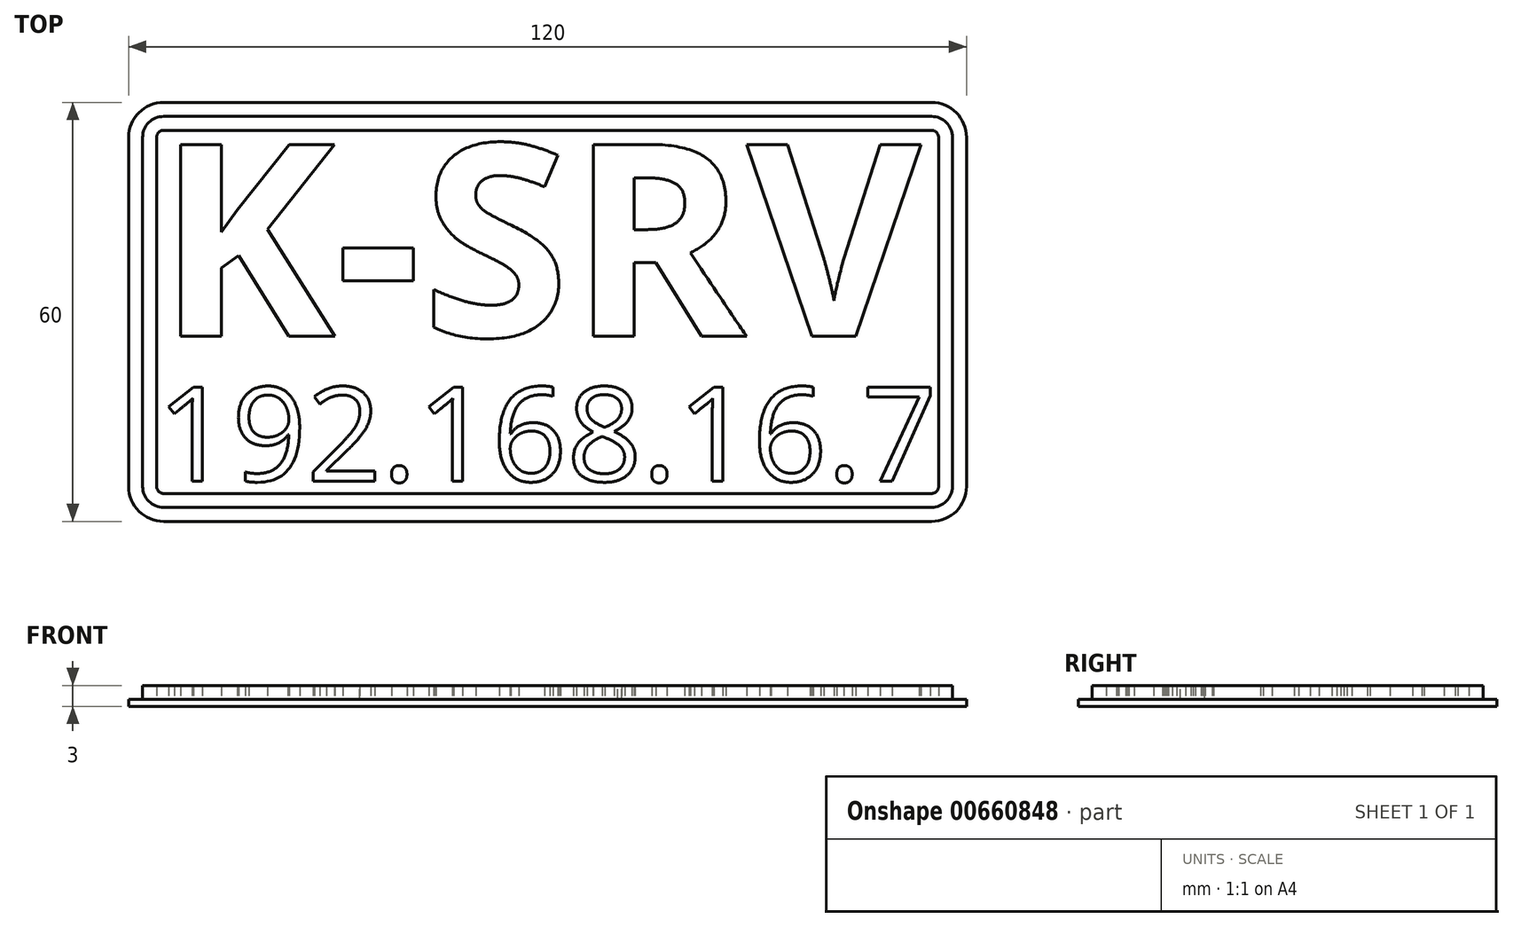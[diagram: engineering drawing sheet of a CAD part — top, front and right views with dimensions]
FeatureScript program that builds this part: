
annotation { "Feature Type Name" : "Feature", "Feature Type Description" : "" }
export const myFeature = defineFeature(function(context is Context, id is Id, definition is map)
    precondition{}
    {
        {
            assignVariable(context, id + "F0", {"variableType" : VariableType.LENGTH, "name" : "st", "lengthValue" : 1 * mm});
        }
        {
            assignVariable(context, id + "F1", {"variableType" : VariableType.LENGTH, "name" : "ft", "lengthValue" : 2 * mm});
        }
        {
            var Q0;
            Q0=qCreatedBy(makeId("Top.planeOp"),FACE);
            var sketch = newSketch(context, id + "F2", { "sketchPlane" : qUnion([Q0])});
            skLineSegment(sketch, "E0.bottom", {"start": v(-55, 30) * mm, "end": v(55, 30) * mm});
            skLineSegment(sketch, "E0.top", {"start": v(-55, -30) * mm, "end": v(55, -30) * mm});
            skLineSegment(sketch, "E0.left", {"start": v(-60, 25) * mm, "end": v(-60, -25) * mm});
            skLineSegment(sketch, "E0.right", {"start": v(60, 25) * mm, "end": v(60, -25) * mm});
            skPoint(sketch, "E1", {"position": v(0, 30) * mm});
            skPoint(sketch, "E2", {"position": v(-60, 0) * mm});
            skPoint(sketch, "E3.visualSharp", {"position": v(-60, 30) * mm});
            skArc(sketch, "E3.filletArc", {"start": v(-55, 30) * mm, "mid": v(-58.54, 28.54) * mm, "end": v(-60, 25) * mm});
            skPoint(sketch, "E4.visualSharp", {"position": v(60, 30) * mm});
            skArc(sketch, "E4.filletArc", {"start": v(60, 25) * mm, "mid": v(58.54, 28.54) * mm, "end": v(55, 30) * mm});
            skPoint(sketch, "E5.visualSharp", {"position": v(60, -30) * mm});
            skArc(sketch, "E5.filletArc", {"start": v(55, -30) * mm, "mid": v(58.54, -28.54) * mm, "end": v(60, -25) * mm});
            skPoint(sketch, "E6.visualSharp", {"position": v(-60, -30) * mm});
            skArc(sketch, "E6.filletArc", {"start": v(-60, -25) * mm, "mid": v(-58.54, -28.54) * mm, "end": v(-55, -30) * mm});
            skSolve(sketch);
        }
        {
            var Q0;
            Q0=qSketchRegion(id+"F2",true);
            extrude(context, id + "F3", {"entities" : qUnion([Q0]), "depth" : getVariable(context, 'st'), "offsetDistance" : 25 * mm});
        }
        {
            var Q0;
            Q0=makeQuery(id+"F3.opExtrude","CAP_FACE",FACE,{"disambiguationData":[OSD([sQuery(id+"F2.wireOp",EDGE,"E0.bottom"),sQuery(id+"F2.wireOp",EDGE,"E0.top"),sQuery(id+"F2.wireOp",EDGE,"E0.left"),sQuery(id+"F2.wireOp",EDGE,"E0.right"),sQuery(id+"F2.wireOp",EDGE,"E3.filletArc"),sQuery(id+"F2.wireOp",EDGE,"E4.filletArc"),sQuery(id+"F2.wireOp",EDGE,"E5.filletArc"),sQuery(id+"F2.wireOp",EDGE,"E6.filletArc")])],"isStart":false});
            var sketch = newSketch(context, id + "F4", { "sketchPlane" : qUnion([Q0])});
            skArc(sketch, "E7.0", {"start": v(-55, 28) * mm, "mid": v(-57.12, 27.12) * mm, "end": v(-58, 25) * mm});
            skLineSegment(sketch, "E7.1", {"start": v(-55, 28) * mm, "end": v(55, 28) * mm});
            skLineSegment(sketch, "E7.2", {"start": v(-58, 25) * mm, "end": v(-58, -25) * mm});
            skArc(sketch, "E7.3", {"start": v(58, 25) * mm, "mid": v(57.12, 27.12) * mm, "end": v(55, 28) * mm});
            skArc(sketch, "E7.4", {"start": v(-58, -25) * mm, "mid": v(-57.12, -27.12) * mm, "end": v(-55, -28) * mm});
            skLineSegment(sketch, "E7.5", {"start": v(-55, -28) * mm, "end": v(55, -28) * mm});
            skArc(sketch, "E7.6", {"start": v(55, -28) * mm, "mid": v(57.12, -27.12) * mm, "end": v(58, -25) * mm});
            skLineSegment(sketch, "E7.7", {"start": v(58, 25) * mm, "end": v(58, -25) * mm});
            skArc(sketch, "E8.0", {"start": v(-55, 26) * mm, "mid": v(-55.7, 25.7) * mm, "end": v(-56, 25) * mm});
            skLineSegment(sketch, "E8.1", {"start": v(-55, 26) * mm, "end": v(55, 26) * mm});
            skLineSegment(sketch, "E8.2", {"start": v(-56, 25) * mm, "end": v(-56, -25) * mm});
            skArc(sketch, "E8.3", {"start": v(56, 25) * mm, "mid": v(55.7, 25.7) * mm, "end": v(55, 26) * mm});
            skArc(sketch, "E8.4", {"start": v(-56, -25) * mm, "mid": v(-55.7, -25.7) * mm, "end": v(-55, -26) * mm});
            skLineSegment(sketch, "E8.5", {"start": v(-55, -26) * mm, "end": v(55, -26) * mm});
            skArc(sketch, "E8.6", {"start": v(55, -26) * mm, "mid": v(55.7, -25.7) * mm, "end": v(56, -25) * mm});
            skLineSegment(sketch, "E8.7", {"start": v(56, 25) * mm, "end": v(56, -25) * mm});
            skText(sketch, "E9", { "text": "K-SRV", "fontName": "OpenSans-Bold.ttf"});
            skText(sketch, "E10", { "text": "192.168.16.7", "fontName": "OpenSans-Regular.ttf"});
            skLineSegment(sketch, "E11", {"start": v(0, -24.22) * mm, "end": v(0, 24.22) * mm, "construction": true});
            const initialGuessF4  = {"E9": [-0.056, -0.00348, 1, 0, 0.0277], "E10": [-0.056, -0.02422, 1, 0, 0.01354]};
            skSetInitialGuess(sketch, initialGuessF4);
            skSolve(sketch);
        }
        {
            var Q0;
            Q0=makeQuery(id+"F4.imprint","IMPRINT",FACE,{"disambiguationData":[TD([[makeQuery(id+"F4.imprint","IMPRINT",EDGE,{"derivedFrom":sQuery(id+"F4.wireOp",EDGE,"E10.sketch_text.stroke-215")}),-1.0]])]});
            var Q1;
            Q1=makeQuery(id+"F4.imprint","IMPRINT",FACE,{"disambiguationData":[TD([[makeQuery(id+"F4.imprint","IMPRINT",EDGE,{"derivedFrom":sQuery(id+"F4.wireOp",EDGE,"E10.sketch_text.stroke-198")}),-1.0]])]});
            var Q2;
            Q2=makeQuery(id+"F4.imprint","IMPRINT",FACE,{"disambiguationData":[TD([[makeQuery(id+"F4.imprint","IMPRINT",EDGE,{"derivedFrom":sQuery(id+"F4.wireOp",EDGE,"E10.sketch_text.stroke-178")}),-1.0]])]});
            var Q3;
            Q3=makeQuery(id+"F4.imprint","IMPRINT",FACE,{"disambiguationData":[TD([[makeQuery(id+"F4.imprint","IMPRINT",EDGE,{"derivedFrom":sQuery(id+"F4.wireOp",EDGE,"E10.sketch_text.stroke-170")}),-1.0]])]});
            var Q4;
            Q4=makeQuery(id+"F4.imprint","IMPRINT",FACE,{"disambiguationData":[TD([[makeQuery(id+"F4.imprint","IMPRINT",EDGE,{"derivedFrom":sQuery(id+"F4.wireOp",EDGE,"E10.sketch_text.stroke-145")}),-1.0]])]});
            var Q5;
            Q5=makeQuery(id+"F4.imprint","IMPRINT",FACE,{"disambiguationData":[TD([[makeQuery(id+"F4.imprint","IMPRINT",EDGE,{"derivedFrom":sQuery(id+"F4.wireOp",EDGE,"E10.sketch_text.stroke-136")}),-1.0]])]});
            var Q6;
            Q6=makeQuery(id+"F4.imprint","IMPRINT",FACE,{"disambiguationData":[TD([[makeQuery(id+"F4.imprint","IMPRINT",EDGE,{"derivedFrom":sQuery(id+"F4.wireOp",EDGE,"E10.sketch_text.stroke-128")}),-1.0]])]});
            var Q7;
            Q7=makeQuery(id+"F4.imprint","IMPRINT",FACE,{"disambiguationData":[TD([[makeQuery(id+"F4.imprint","IMPRINT",EDGE,{"derivedFrom":sQuery(id+"F4.wireOp",EDGE,"E10.sketch_text.stroke-97")}),-1.0]])]});
            var Q8;
            Q8=makeQuery(id+"F4.imprint","IMPRINT",FACE,{"disambiguationData":[TD([[makeQuery(id+"F4.imprint","IMPRINT",EDGE,{"derivedFrom":sQuery(id+"F4.wireOp",EDGE,"E10.sketch_text.stroke-72")}),-1.0]])]});
            var Q9;
            Q9=makeQuery(id+"F4.imprint","IMPRINT",FACE,{"disambiguationData":[TD([[makeQuery(id+"F4.imprint","IMPRINT",EDGE,{"derivedFrom":sQuery(id+"F4.wireOp",EDGE,"E10.sketch_text.stroke-0")}),-1.0]])]});
            var Q10;
            Q10=makeQuery(id+"F4.imprint","IMPRINT",FACE,{"disambiguationData":[TD([[makeQuery(id+"F4.imprint","IMPRINT",EDGE,{"derivedFrom":sQuery(id+"F4.wireOp",EDGE,"E10.sketch_text.stroke-9")}),-1.0]])]});
            var Q11;
            Q11=makeQuery(id+"F4.imprint","IMPRINT",FACE,{"disambiguationData":[TD([[makeQuery(id+"F4.imprint","IMPRINT",EDGE,{"derivedFrom":sQuery(id+"F4.wireOp",EDGE,"E10.sketch_text.stroke-35")}),-1.0]])]});
            var Q12;
            Q12=makeQuery(id+"F4.imprint","IMPRINT",FACE,{"disambiguationData":[TD([[makeQuery(id+"F4.imprint","IMPRINT",EDGE,{"derivedFrom":sQuery(id+"F4.wireOp",EDGE,"E10.sketch_text.stroke-55")}),-1.0]])]});
            var Q13;
            Q13=makeQuery(id+"F4.imprint","IMPRINT",FACE,{"disambiguationData":[TD([[makeQuery(id+"F4.imprint","IMPRINT",EDGE,{"derivedFrom":sQuery(id+"F4.wireOp",EDGE,"E10.sketch_text.stroke-63")}),-1.0]])]});
            var Q14;
            Q14=makeQuery(id+"F4.imprint","IMPRINT",FACE,{"disambiguationData":[TD([[makeQuery(id+"F4.imprint","IMPRINT",EDGE,{"derivedFrom":sQuery(id+"F4.wireOp",EDGE,"E9.sketch_text.stroke-0")}),-1.0]])]});
            var Q15;
            Q15=makeQuery(id+"F4.imprint","IMPRINT",FACE,{"disambiguationData":[TD([[makeQuery(id+"F4.imprint","IMPRINT",EDGE,{"derivedFrom":sQuery(id+"F4.wireOp",EDGE,"E7.0")}),1.0]])]});
            var Q16;
            Q16=makeQuery(id+"F4.imprint","IMPRINT",FACE,{"disambiguationData":[TD([[makeQuery(id+"F4.imprint","IMPRINT",EDGE,{"derivedFrom":sQuery(id+"F4.wireOp",EDGE,"E9.sketch_text.stroke-13")}),-1.0]])]});
            var Q17;
            Q17=makeQuery(id+"F4.imprint","IMPRINT",FACE,{"disambiguationData":[TD([[makeQuery(id+"F4.imprint","IMPRINT",EDGE,{"derivedFrom":sQuery(id+"F4.wireOp",EDGE,"E9.sketch_text.stroke-41")}),-1.0]])]});
            var Q18;
            Q18=makeQuery(id+"F4.imprint","IMPRINT",FACE,{"disambiguationData":[TD([[makeQuery(id+"F4.imprint","IMPRINT",EDGE,{"derivedFrom":sQuery(id+"F4.wireOp",EDGE,"E9.sketch_text.stroke-45")}),-1.0]])]});
            var Q19;
            Q19=makeQuery(id+"F4.imprint","IMPRINT",FACE,{"disambiguationData":[TD([[makeQuery(id+"F4.imprint","IMPRINT",EDGE,{"derivedFrom":sQuery(id+"F4.wireOp",EDGE,"E9.sketch_text.stroke-57")}),-1.0]])]});
            var Q20;
            Q20=makeQuery(id+"F4.imprint","IMPRINT",FACE,{"disambiguationData":[TD([[makeQuery(id+"F4.imprint","IMPRINT",EDGE,{"derivedFrom":sQuery(id+"F4.wireOp",EDGE,"E9.sketch_text.stroke-76")}),-1.0]])]});
            var Q21;
            Q21=makeQuery(id+"F4.imprint","IMPRINT",FACE,{"disambiguationData":[TD([[makeQuery(id+"F4.imprint","IMPRINT",EDGE,{"derivedFrom":sQuery(id+"F4.wireOp",EDGE,"E9.sketch_text.stroke-64")}),-1.0]])]});
            extrude(context, id + "F5", {"entities" : qUnion([Q0, Q1, Q2, Q3, Q4, Q5, Q6, Q7, Q8, Q9, Q10, Q11, Q12, Q13, Q14, Q15, Q16, Q17, Q18, Q19, Q20, Q21]), "operationType" : NewBodyOperationType.ADD, "depth" : getVariable(context, 'ft'), "offsetDistance" : 25 * mm});
        }
    });
